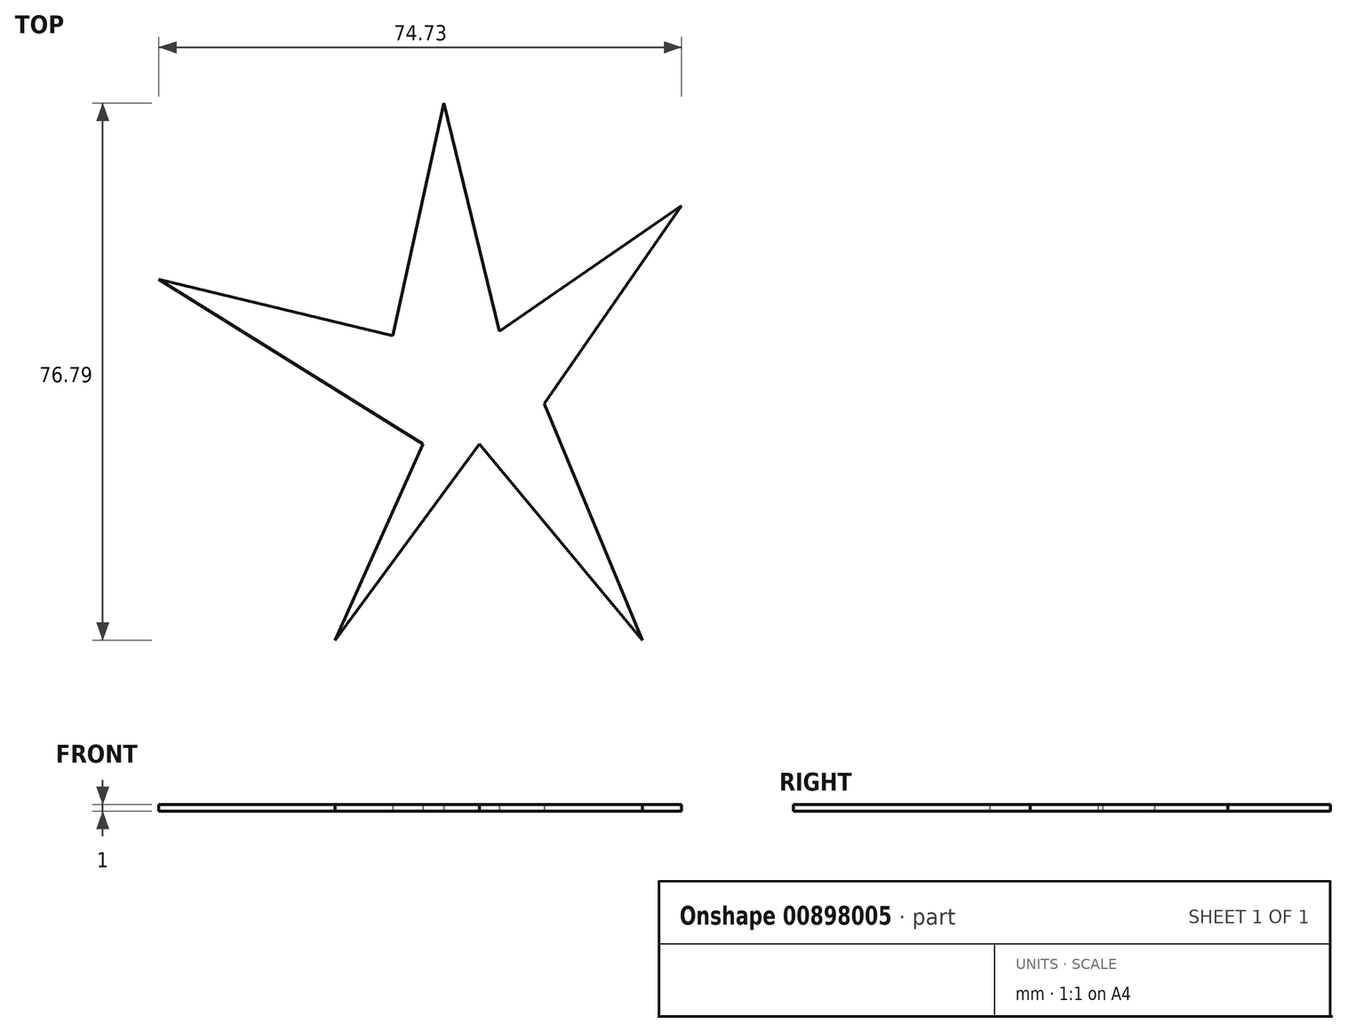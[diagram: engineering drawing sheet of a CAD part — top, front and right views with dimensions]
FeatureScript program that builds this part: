
annotation { "Feature Type Name" : "Feature", "Feature Type Description" : "" }
export const myFeature = defineFeature(function(context is Context, id is Id, definition is map)
    precondition{}
    {
        {
            var Q0;
            Q0=qCreatedBy(makeId("Top.planeOp"),FACE);
            var sketch = newSketch(context, id + "F0", { "sketchPlane" : qUnion([Q0])});
            skLineSegment(sketch, "E0", {"start": v(-7.33, 15.48) * mm, "end": v(0, 48.72) * mm});
            skLineSegment(sketch, "E1", {"start": v(0, 48.72) * mm, "end": v(7.95, 16.1) * mm});
            skLineSegment(sketch, "E2", {"start": v(7.95, 16.1) * mm, "end": v(33.96, 34.06) * mm});
            skLineSegment(sketch, "E3", {"start": v(33.96, 34.06) * mm, "end": v(14.35, 5.78) * mm});
            skLineSegment(sketch, "E4", {"start": v(14.35, 5.78) * mm, "end": v(28.38, -28.07) * mm});
            skLineSegment(sketch, "E5", {"start": v(28.38, -28.07) * mm, "end": v(5.06, 0) * mm});
            skLineSegment(sketch, "E6", {"start": v(5.06, 0) * mm, "end": v(-15.58, -28.07) * mm});
            skLineSegment(sketch, "E7", {"start": v(-15.58, -28.07) * mm, "end": v(-3, 0) * mm});
            skLineSegment(sketch, "E8", {"start": v(-3, 0) * mm, "end": v(-40.77, 23.53) * mm});
            skLineSegment(sketch, "E9", {"start": v(-40.77, 23.53) * mm, "end": v(-7.33, 15.48) * mm});
            skSolve(sketch);
        }
        {
            var Q0;
            Q0=qCreatedBy(makeId("Top.planeOp"),FACE);
            var sketch = newSketch(context, id + "F1", { "sketchPlane" : qUnion([Q0])});
            skSolve(sketch);
        }
        {
            var Q0;
            Q0 = qSketchRegion(id + "F1", true);
            var Q1;
            Q1=makeQuery(id+"F0.imprint","IMPRINT",FACE,{"disambiguationData":[TD([[makeQuery(id+"F0.imprint","IMPRINT",EDGE,{"derivedFrom":sQuery(id+"F0.wireOp",EDGE,"E0")}),-1.0]])]});
            extrude(context, id + "F2", {"entities" : qUnion([Q0, Q1]), "depth" : 1 * mm, "offsetDistance" : 25 * mm});
        }
    });
